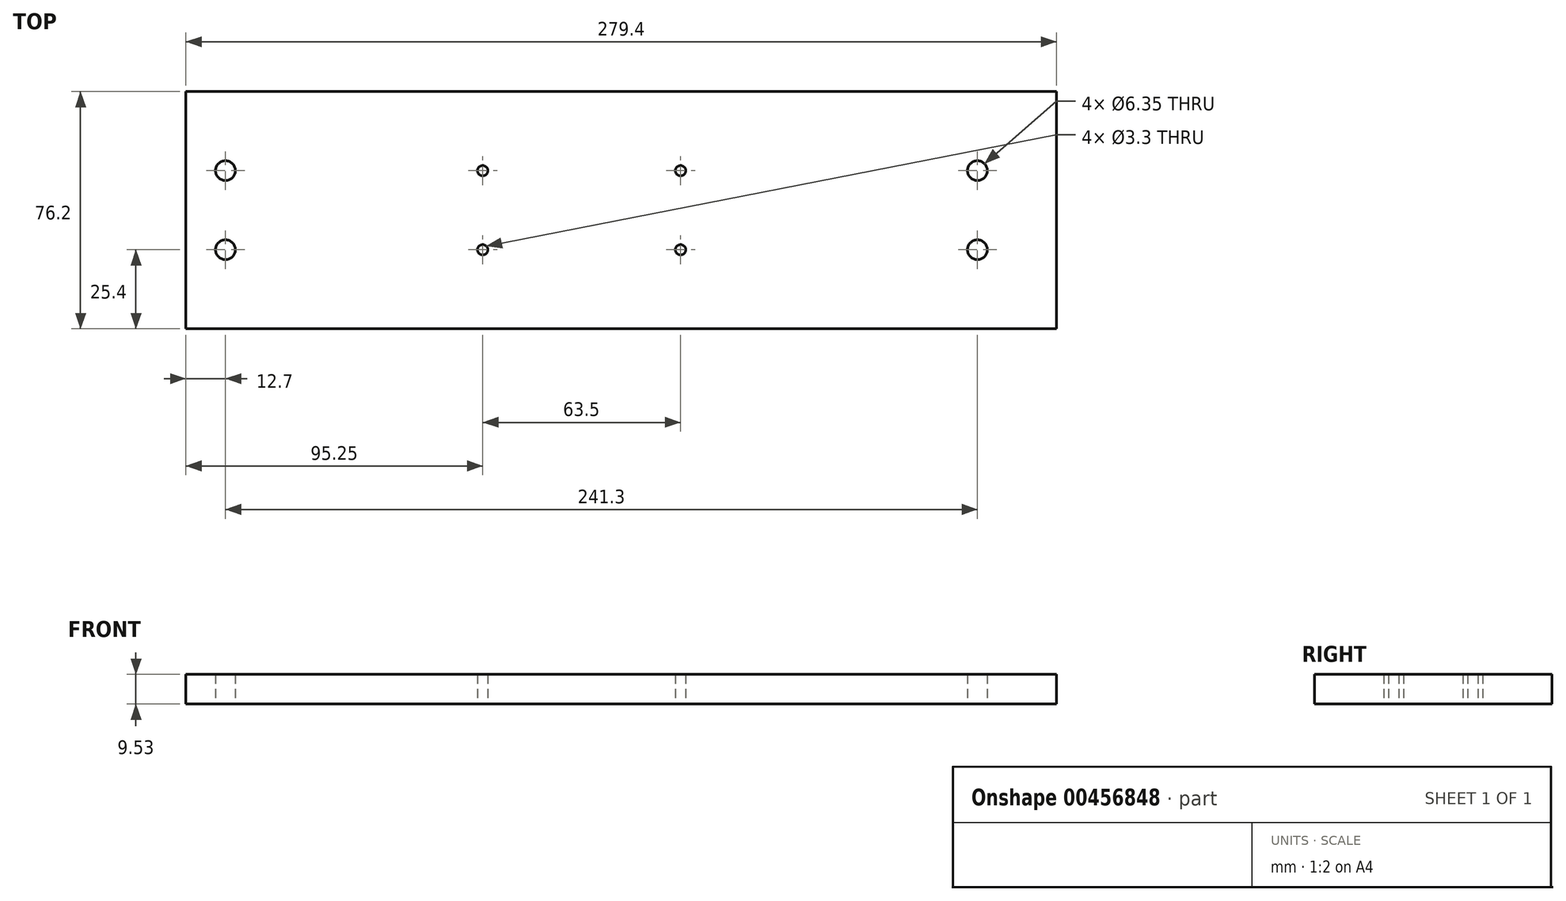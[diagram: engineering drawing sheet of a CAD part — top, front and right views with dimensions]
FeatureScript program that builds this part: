
annotation { "Feature Type Name" : "Feature", "Feature Type Description" : "" }
export const myFeature = defineFeature(function(context is Context, id is Id, definition is map)
    precondition{}
    {
        {
            var Q0;
            Q0=qCreatedBy(makeId("Top.planeOp"),FACE);
            var sketch = newSketch(context, id + "F0", { "sketchPlane" : qUnion([Q0])});
            skLineSegment(sketch, "E0.bottom", {"start": v(0, -38.1) * mm, "end": v(279.4, -38.1) * mm});
            skLineSegment(sketch, "E0.top", {"start": v(0, 38.1) * mm, "end": v(279.4, 38.1) * mm});
            skLineSegment(sketch, "E0.left", {"start": v(0, -38.1) * mm, "end": v(0, 38.1) * mm});
            skLineSegment(sketch, "E0.right", {"start": v(279.4, -38.1) * mm, "end": v(279.4, 38.1) * mm});
            skCircle(sketch, "E1", {"center": v(12.7, 12.7) * mm, "radius": 3.18 * mm});
            skCircle(sketch, "E2", {"center": v(12.7, -12.7) * mm, "radius": 3.18 * mm});
            skCircle(sketch, "E3", {"center": v(95.25, -12.7) * mm, "radius": 1.65 * mm});
            skCircle(sketch, "E4", {"center": v(95.25, 12.7) * mm, "radius": 1.65 * mm});
            skCircle(sketch, "E5", {"center": v(158.75, 12.7) * mm, "radius": 1.65 * mm});
            skCircle(sketch, "E6", {"center": v(158.75, -12.7) * mm, "radius": 1.65 * mm});
            skCircle(sketch, "E7", {"center": v(254, -12.7) * mm, "radius": 3.18 * mm});
            skCircle(sketch, "E8", {"center": v(254, 12.7) * mm, "radius": 3.18 * mm});
            skSolve(sketch);
        }
        {
            var Q0;
            Q0=makeQuery(id+"F0.imprint","IMPRINT",FACE,{"disambiguationData":[TD([[makeQuery(id+"F0.imprint","IMPRINT",EDGE,{"derivedFrom":sQuery(id+"F0.wireOp",EDGE,"E0.bottom")}),1.0]])]});
            extrude(context, id + "F1", {"entities" : qUnion([Q0]), "depth" : 9.52 * mm});
        }
    });
